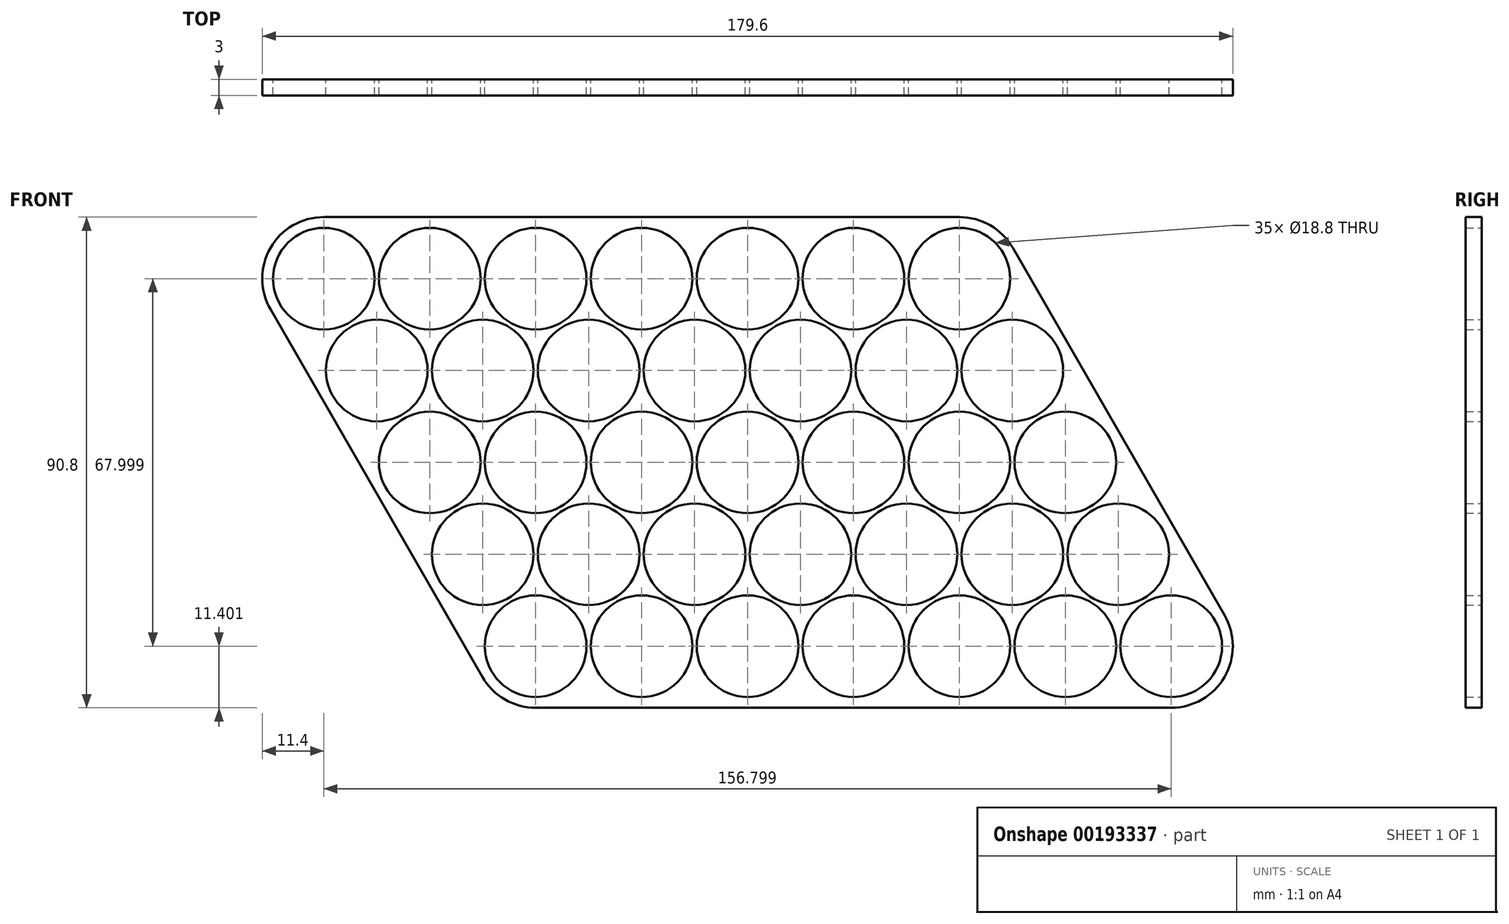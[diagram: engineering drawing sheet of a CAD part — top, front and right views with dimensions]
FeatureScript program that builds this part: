
annotation { "Feature Type Name" : "Feature", "Feature Type Description" : "" }
export const myFeature = defineFeature(function(context is Context, id is Id, definition is map)
    precondition{}
    {
        {
            var Q0;
            Q0=qCreatedBy(makeId("Front.planeOp"),FACE);
            var sketch = newSketch(context, id + "F0", { "sketchPlane" : qUnion([Q0])});
            skCircle(sketch, "E0", {"center": v(0, 0) * mm, "radius": 9.4 * mm});
            skCircle(sketch, "E1.1.0.0", {"center": v(19.6, 0) * mm, "radius": 9.4 * mm});
            skCircle(sketch, "E1.2.0.0", {"center": v(39.2, 0) * mm, "radius": 9.4 * mm});
            skCircle(sketch, "E1.3.0.0", {"center": v(58.8, 0) * mm, "radius": 9.4 * mm});
            skLineSegment(sketch, "E1.direction1", {"start": v(0, 0) * mm, "end": v(19.6, 0) * mm, "construction": true});
            skLineSegment(sketch, "E2", {"start": v(0, -17) * mm, "end": v(73.2, -17) * mm, "construction": true});
            skLineSegment(sketch, "E3", {"start": v(9.8, 0) * mm, "end": v(9.8, -17) * mm, "construction": true});
            skCircle(sketch, "E4", {"center": v(9.8, -17) * mm, "radius": 9.4 * mm});
            skCircle(sketch, "E5.1.0.0", {"center": v(29.4, -17) * mm, "radius": 9.4 * mm});
            skCircle(sketch, "E5.2.0.0", {"center": v(49, -17) * mm, "radius": 9.4 * mm});
            skCircle(sketch, "E5.3.0.0", {"center": v(68.6, -17) * mm, "radius": 9.4 * mm});
            skLineSegment(sketch, "E5.direction1", {"start": v(9.8, -17) * mm, "end": v(29.4, -17) * mm, "construction": true});
            skLineSegment(sketch, "E6", {"start": v(-8.14, -4.7) * mm, "end": v(1.66, -21.7) * mm});
            skLineSegment(sketch, "E7", {"start": v(0, 9.4) * mm, "end": v(58.8, 9.4) * mm});
            skLineSegment(sketch, "E8", {"start": v(9.8, -17) * mm, "end": v(9.8, -26.4) * mm, "construction": true});
            skLineSegment(sketch, "E9", {"start": v(68.6, -17) * mm, "end": v(68.6, -26.4) * mm, "construction": true});
            skArc(sketch, "E10", {"start": v(58.8, 9.4) * mm, "mid": v(63.5, 8.14) * mm, "end": v(66.94, 4.7) * mm});
            skArc(sketch, "E11", {"start": v(76.74, -12.3) * mm, "mid": v(76.74, -21.7) * mm, "end": v(68.6, -26.4) * mm});
            skArc(sketch, "E12", {"start": v(9.8, -26.4) * mm, "mid": v(5.1, -25.14) * mm, "end": v(1.66, -21.7) * mm});
            skArc(sketch, "E13", {"start": v(-8.14, -4.7) * mm, "mid": v(-8.14, 4.7) * mm, "end": v(0, 9.4) * mm});
            skArc(sketch, "E14.0", {"start": v(0, 11.4) * mm, "mid": v(-9.87, 5.7) * mm, "end": v(-9.88, -5.7) * mm});
            skLineSegment(sketch, "E15.0", {"start": v(0, 11.4) * mm, "end": v(58.8, 11.4) * mm});
            skLineSegment(sketch, "E16.0", {"start": v(-9.88, -5.7) * mm, "end": v(-0.08, -22.7) * mm});
            skArc(sketch, "E17.trimOffspring", {"start": v(9.8, -5.82) * mm, "mid": v(9.87, -5.71) * mm, "end": v(9.93, -5.6) * mm});
            skArc(sketch, "E18.trimOffspring", {"start": v(9.93, -5.6) * mm, "mid": v(9.86, -5.6) * mm, "end": v(9.8, -5.6) * mm});
            skCircle(sketch, "E19.0.4.0", {"center": v(78.4, 0) * mm, "radius": 9.4 * mm});
            skCircle(sketch, "E19.0.5.0", {"center": v(98, 0) * mm, "radius": 9.4 * mm});
            skCircle(sketch, "E20.0.4.0", {"center": v(88.2, -17) * mm, "radius": 9.4 * mm});
            skCircle(sketch, "E20.0.5.0", {"center": v(107.8, -17) * mm, "radius": 9.4 * mm});
            skLineSegment(sketch, "E21", {"start": v(58.8, 11.4) * mm, "end": v(98, 11.4) * mm});
            skLineSegment(sketch, "E22", {"start": v(0, 0) * mm, "end": v(9.8, -17) * mm, "construction": true});
            skCircle(sketch, "E23.1.0.0", {"center": v(19.6, -34) * mm, "radius": 9.4 * mm});
            skCircle(sketch, "E23.2.0.0", {"center": v(29.4, -51) * mm, "radius": 9.4 * mm});
            skLineSegment(sketch, "E23.direction1", {"start": v(9.8, -17) * mm, "end": v(19.6, -34) * mm, "construction": true});
            skCircle(sketch, "E24.1.0.0", {"center": v(39.2, -34) * mm, "radius": 9.4 * mm});
            skCircle(sketch, "E24.1.0.1", {"center": v(49, -51) * mm, "radius": 9.4 * mm});
            skCircle(sketch, "E24.2.0.0", {"center": v(58.8, -34) * mm, "radius": 9.4 * mm});
            skCircle(sketch, "E24.2.0.1", {"center": v(68.6, -51) * mm, "radius": 9.4 * mm});
            skCircle(sketch, "E24.3.0.0", {"center": v(78.4, -34) * mm, "radius": 9.4 * mm});
            skCircle(sketch, "E24.3.0.1", {"center": v(88.2, -51) * mm, "radius": 9.4 * mm});
            skCircle(sketch, "E24.4.0.0", {"center": v(98, -34) * mm, "radius": 9.4 * mm});
            skCircle(sketch, "E24.4.0.1", {"center": v(107.8, -51) * mm, "radius": 9.4 * mm});
            skCircle(sketch, "E24.5.0.0", {"center": v(117.6, -34) * mm, "radius": 9.4 * mm});
            skCircle(sketch, "E24.5.0.1", {"center": v(127.4, -51) * mm, "radius": 9.4 * mm});
            skLineSegment(sketch, "E24.direction1", {"start": v(19.6, -34) * mm, "end": v(39.2, -34) * mm, "construction": true});
            skLineSegment(sketch, "E25", {"start": v(-0.08, -22.7) * mm, "end": v(19.52, -56.7) * mm});
            skArc(sketch, "E26.0", {"start": v(29.27, -62.4) * mm, "mid": v(29.33, -62.4) * mm, "end": v(29.4, -62.4) * mm});
            skCircle(sketch, "E27.0.6.0", {"center": v(117.6, 0) * mm, "radius": 9.4 * mm});
            skCircle(sketch, "E28.0.6.0", {"center": v(127.4, -17) * mm, "radius": 9.4 * mm});
            skCircle(sketch, "E29.0.6.0", {"center": v(137.2, -34) * mm, "radius": 9.4 * mm});
            skCircle(sketch, "E29.2.6.0", {"center": v(147, -51) * mm, "radius": 9.4 * mm});
            skLineSegment(sketch, "E30", {"start": v(98, 11.4) * mm, "end": v(117.6, 11.4) * mm});
            skCircle(sketch, "E31.0.3.0", {"center": v(39.2, -68) * mm, "radius": 9.4 * mm});
            skCircle(sketch, "E32.1.0.0", {"center": v(58.8, -68) * mm, "radius": 9.4 * mm});
            skCircle(sketch, "E32.2.0.0", {"center": v(78.4, -68) * mm, "radius": 9.4 * mm});
            skCircle(sketch, "E32.3.0.0", {"center": v(98, -68) * mm, "radius": 9.4 * mm});
            skCircle(sketch, "E32.4.0.0", {"center": v(117.6, -68) * mm, "radius": 9.4 * mm});
            skCircle(sketch, "E32.5.0.0", {"center": v(137.2, -68) * mm, "radius": 9.4 * mm});
            skCircle(sketch, "E32.6.0.0", {"center": v(156.8, -68) * mm, "radius": 9.4 * mm});
            skLineSegment(sketch, "E32.direction1", {"start": v(39.2, -68) * mm, "end": v(58.8, -68) * mm, "construction": true});
            skArc(sketch, "E33.0", {"start": v(29.32, -73.7) * mm, "mid": v(33.5, -77.87) * mm, "end": v(39.2, -79.4) * mm});
            skLineSegment(sketch, "E34", {"start": v(19.52, -56.7) * mm, "end": v(29.32, -73.7) * mm});
            skLineSegment(sketch, "E35", {"start": v(39.2, -79.4) * mm, "end": v(156.8, -79.4) * mm});
            skArc(sketch, "E36", {"start": v(127.48, 5.7) * mm, "mid": v(123.3, 9.87) * mm, "end": v(117.6, 11.4) * mm});
            skArc(sketch, "E37", {"start": v(156.8, -79.4) * mm, "mid": v(166.67, -73.7) * mm, "end": v(166.68, -62.3) * mm});
            skLineSegment(sketch, "E38", {"start": v(127.48, 5.7) * mm, "end": v(166.68, -62.3) * mm});
            skSolve(sketch);
        }
        {
            var Q0;
            Q0=qSketchRegion(id+"F0",true);
            var Q1;
            {var subQ3=sQuery(id+"F0.wireOp",EDGE,"E1.1.0.0");Q1=makeQuery(id+"F0.imprint","IMPRINT",FACE,{"disambiguationData":[TD([[makeQuery(id+"F0.imprint","IMPRINT",EDGE,{"derivedFrom":subQ3}),-1.0]])]});}
            extrude(context, id + "F1", {"entities" : qUnion([Q0, Q1]), "depth" : 3 * mm});
        }
    });
